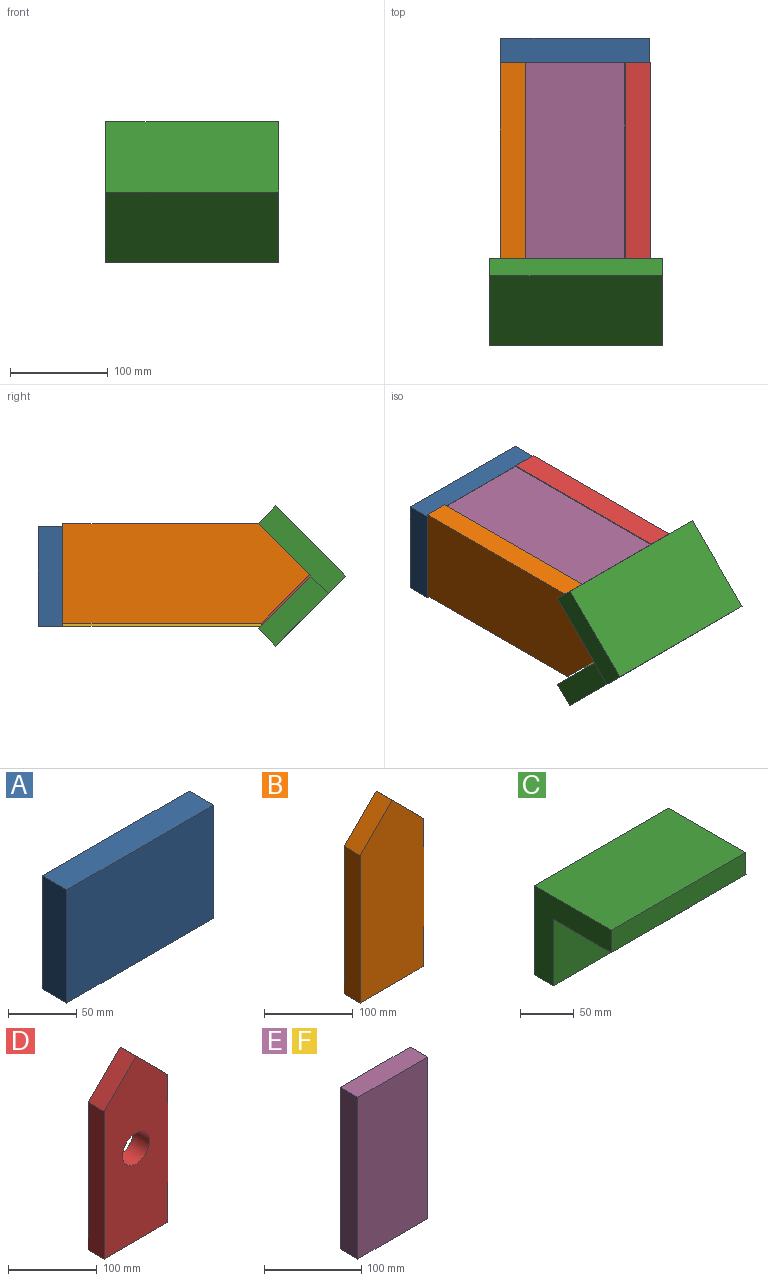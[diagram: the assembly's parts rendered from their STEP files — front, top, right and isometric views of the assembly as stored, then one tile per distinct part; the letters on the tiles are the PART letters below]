
ASSEMBLY  parts=6 mates=5
PART A: 6 faces, bbox 152.4x25.4x101.6 mm
  f0: plane 152.4x25.4mm, normal (0,0,-1), area 3871mm2, adj f1,f2,f4,f5
  f1: plane 101.6x25.4mm, normal (1,0,0), area 2580.6mm2, adj f0,f3,f4,f5
  f2: plane 101.6x25.4mm, normal (-1,0,0), area 2580.6mm2, adj f0,f3,f4,f5
  f3: plane 152.4x25.4mm, normal (0,0,1), area 3871mm2, adj f1,f2,f4,f5
  f4: plane 152.4x101.6mm, normal (0,-1,0), area 15483.8mm2, adj f0,f1,f2,f3
  f5: plane 152.4x101.6mm, normal (0,1,0), area 15483.8mm2, adj f0,f1,f2,f3
PART B: 7 faces, bbox 101.6x25.4x254 mm
  f0: plane 203.2x25.4mm, normal (-1,0,0), area 5161.3mm2, adj f1,f4,f5,f6
  f1: plane 101.6x25.4mm, normal (0,0,-1), area 2580.6mm2, adj f0,f2,f5,f6
  f2: plane 203.2x25.4mm, normal (1,0,0), area 5161.3mm2, adj f1,f3,f5,f6
  f3: plane 50.8x50.8mm, normal (0.71,0,0.71), area 1824.8mm2, adj f2,f4,f5,f6
  f4: plane 50.8x50.8mm, normal (-0.71,0,0.71), area 1824.8mm2, adj f0,f3,f5,f6
  f5: plane 254x101.6mm, normal (0,-1,0), area 23225.8mm2, adj f0,f1,f2,f3,f4
  f6: plane 254x101.6mm, normal (0,1,0), area 23225.8mm2, adj f0,f1,f2,f3,f4
PART C: 9 faces, bbox 177.8x101.6x101.6 mm
  f0: plane 101.6x101.59mm, normal (-1,0,0), area 4515.6mm2, adj f1,f3,f4,f5,f7,f8
  f1: plane 177.8x25.4mm, normal (0,0,-1), area 4516.1mm2, adj f0,f2,f3,f4
  f2: plane 76.2x25.4mm, normal (1,0,0), area 1935.5mm2, adj f1,f3,f4,f6
  f3: plane 177.8x76.2mm, normal (0,-1,0), area 13548.4mm2, adj f0,f1,f2,f5
  f4: plane 177.8x101.59mm, normal (0,1,0), area 18056.8mm2, adj f0,f1,f2,f6,f7
  f5: plane 177.8x76.2mm, normal (0,0,-1), area 13548.4mm2, adj f0,f3,f6,f8
  f6: plane 101.6x25.39mm, normal (1,0,0.02), area 2580.6mm2, adj f2,f4,f5,f7,f8
  f7: plane 177.27x101.6mm, normal (0,0,1), area 18010.7mm2, adj f0,f4,f6,f8
  f8: plane 177.8x25.39mm, normal (0,-1,0), area 4508.4mm2, adj f0,f5,f6,f7
PART D: 8 faces, bbox 101.6x25.4x254 mm
  f0: plane 203.2x25.4mm, normal (-1,0,0), area 5161.3mm2, adj f1,f5,f6,f7
  f1: plane 101.6x25.4mm, normal (0,0,-1), area 2580.6mm2, adj f0,f2,f6,f7
  f2: plane 203.2x25.4mm, normal (1,0,0), area 5161.3mm2, adj f1,f3,f6,f7
  f3: plane 50.8x50.8mm, normal (0.71,0,0.71), area 1824.8mm2, adj f2,f5,f6,f7
  f4: cylinder r=21.41mm len=42.82mm, axis (0,1,0), area 3417.1mm2, adj f6,f7
  f5: plane 50.8x50.8mm, normal (-0.71,0,0.71), area 1824.8mm2, adj f0,f3,f6,f7
  f6: plane 254x101.6mm, normal (0,-1,0), area 21785.5mm2, adj f0,f1,f2,f3,f4,f5
  f7: plane 254x101.6mm, normal (0,1,0), area 21785.5mm2, adj f0,f1,f2,f3,f4,f5
PART E: 6 faces, bbox 101.6x25.4x203.2 mm
  f0: plane 203.2x25.4mm, normal (-1,0,0), area 5161.3mm2, adj f1,f3,f4,f5
  f1: plane 101.6x25.4mm, normal (0,0,-1), area 2580.6mm2, adj f0,f2,f4,f5
  f2: plane 203.2x25.4mm, normal (1,0,0), area 5161.3mm2, adj f1,f3,f4,f5
  f3: plane 101.6x25.4mm, normal (0,0,1), area 2580.6mm2, adj f0,f2,f4,f5
  f4: plane 203.2x101.6mm, normal (0,-1,0), area 20645.1mm2, adj f0,f1,f2,f3
  f5: plane 203.2x101.6mm, normal (0,1,0), area 20645.1mm2, adj f0,f1,f2,f3
PART F: same geometry as E
PLACE A at identity fixed
PLACE B rot(axis=(0.58,-0.58,0.58),120deg) t=(-76.02,-177.81,27.91)mm
PLACE C rot(axis=(0,-0.38,0.92),180deg) t=(5.06,-270.19,-33.12)mm
PLACE D rot(axis=(0.58,-0.58,0.58),120deg) t=(52.4,-122.12,57.64)mm
PLACE E rot(axis=(-1,0,0),90deg) t=(14,-180.22,36.89)mm
PLACE F rot(axis=(1,0,0),90deg) t=(14,-73.78,-13.91)mm
MATE planar F.f1 <-> A.f4  axis (0,1,0) through (0.77,-25.4,-39.31)mm
MATE fastened C.f3 <-> D.f5  axis (0,0.71,0.71) through (90.5,-279.4,12.01)mm
MATE planar B.f1 <-> A.f4  axis (0,1,0) through (-63.32,-25.4,14.56)mm
MATE planar E.f3 <-> A.f4  axis (0,1,0) through (0.77,-25.4,62.29)mm
MATE planar D.f1 <-> A.f4  axis (0,1,0) through (65.1,-25.4,12.01)mm
